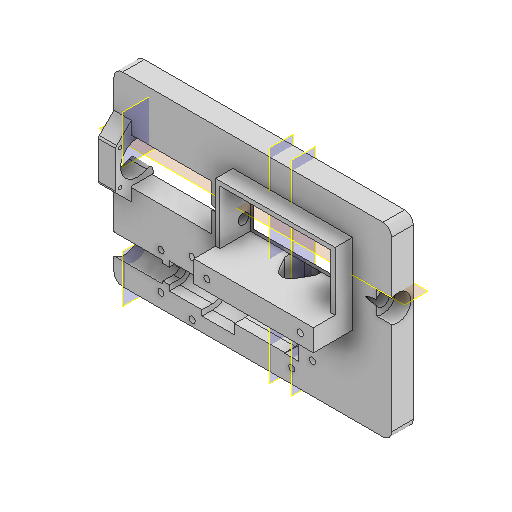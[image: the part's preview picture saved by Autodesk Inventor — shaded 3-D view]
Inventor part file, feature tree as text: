
AUTODESK INVENTOR PART (.ipt)
format: ipt  version: 2022 (Build 260153000, 153)  size: 477,184 bytes
history: native  units: mm
features: sketch x20, extrude x19, reference x11, other x10, plane x8, projected_geometry x7, fillet x2, chamfer x1, mirror x1, hole x1
ambient origin geometry x8: Origin, YZ Plane, XZ Plane, XY Plane, X Axis, Y Axis, Z Axis, Center Point
bodies: Solid1 (feature_tree)
feature tree (80):
  extrude  "Extrusion1"  Depth=10.0mm
  fillet  "Fillet1"  Radius=10.0mm
  extrude  "Extrusion2"  Depth=51.0mm
  extrude  "Extrusion3"  Depth=20.0mm
  plane  "Work Plane1"
  plane  "Work Plane2"
  chamfer  "Chamfer1"  [1 undecoded]
  extrude  "Extrusion4"  Depth=10.0mm
  extrude  "Extrusion5"  Depth=8.0mm
  extrude  "Extrusion6"  Depth=4.0mm TaperAngle=0.0deg
  plane  "Work Plane3"
  extrude  "Extrusion12"  Depth=20.0mm TaperAngle=0.0deg
  extrude  "Extrusion13"  Depth=10.0mm
  mirror  "Mirror1"
  plane  "Work Plane4"
  plane  "Work Plane5"
  extrude  "Extrusion21"  Depth=2.0mm
  extrude  "Extrusion22"  Depth=30.0mm
  plane  "Arbeitsebene7"
  extrude  "Extrusion27"  Depth=7.0mm
  extrude  "Extrusion28"  Depth=10.0mm
  extrude  "Extrusion29"  Depth=6.0mm
  fillet  "Rundung6"  Radius=6.0mm
  sketch  "Skizze32"  dims[d61=30.0mm d62=-0.523599mm d63=12.0mm]
  plane  "Arbeitsebene8"
  extrude  "Extrusion30"  TaperAngle=0.0deg  [1 undecoded]
  extrude  "Extrusion31"  Depth=40.0mm TaperAngle=0.0deg
  extrude  "Extrusion32"  Depth=0.5mm
  extrude  "Extrusion33"  Depth=1.0mm TaperAngle=0.0deg
  sketch  "Skizze36"  dims[d108=6.0mm d109=0.0mm d110=0.0mm]
  plane  "Arbeitsebene9"
  extrude  "Extrusion34"  Depth=8.0mm
  extrude  "Extrusion35"  TaperAngle=45.0deg  [1 undecoded]
  hole  "Bohrung2"  [1 undecoded]
  sketch  "Sketch1"  dims[d0=127.8mm d1=85.5mm d2=10.0mm d3=0.0mm]
  sketch  "Sketch2"  dims[d4=4.0mm d5=51.0mm]
  projected_geometry  "Projected Loop1"
  sketch  "Sketch3"  dims[d6=25.0mm d7=20.0mm]
  projected_geometry  "Projected Loop2"
  sketch  "Sketch4"  dims[d8=15.0mm]
  projected_geometry  "Projected Loop3"
  sketch  "Sketch5"  dims[d9=6.0mm]
  sketch  "Sketch6"  dims[d10=0.0mm]
  reference  "Reference2"
  sketch  "Sketch12"  dims[d11=1.5mm d12=0.0mm d13=0.0mm]
  reference  "Reference4"
  sketch  "Sketch13"  dims[d14=4.0mm d15=2.0mm d16=45.0deg d17=10.0mm]
  sketch  "Sketch22"  dims[d18=8.0mm d19=0.0mm d20=1.9mm]
  projected_geometry  "Projected Loop8"
  sketch  "Sketch23"  dims[d21=4.0mm d22=5.0mm d23=0.0mm]
  projected_geometry  "Projected Loop9"
  reference  "Reference11"
  sketch  "Skizze28"  dims[d27=20.0mm d28=18.0mm d29=0.0mm]
  sketch  "Skizze29"  dims[d38=10.0mm d52=2.0mm]
  reference  "Referenz13"
  sketch  "Skizze30"  dims[d53=2.0mm d54=2.0mm]
  reference  "Referenz14"
  reference  "Referenz16"
  sketch  "Skizze33"  dims[d64=7.0mm d65=0.0mm d100=7.0mm]
  reference  "Referenz17"
  sketch  "Skizze34"  dims[d101=10.0mm d102=0.0mm d103=11.8mm]
  reference  "Referenz18"
  sketch  "Skizze35"  dims[d105=2.8mm d106=2.8mm d107=6.0mm]
  projected_geometry  "Projizierte Kontur15"
  reference  "Referenz19"
  reference  "Referenz20"
  sketch  "Skizze37"  dims[d142=0.5mm d143=40.0mm d144=0.0mm]
  reference  "Referenz21"
  sketch  "Skizze38"  dims[d145=8.0mm d146=0.0mm d147=0.5mm d148=1.0mm d149=0.0mm d150=2.0mm d151=45.0deg d152=45.0deg d153=8.0mm d154=0.0mm d155=7.0mm d156=3.0mm d157=0.0mm d158=30.0mm d159=0.0mm d160=17.0mm d161=15.0mm d162=0.0mm d163=0.5mm d164=15.0mm d165=0.0mm d166=8.0mm d167=10.0mm d168=0.0mm d169=2.8mm d170=6.0mm d171=4.0mm d172=2.0mm d173=90.0deg d174=8.0mm d175=20.594885mm]
  projected_geometry  "Projizierte Kontur16"
  other  "<userpath>\Documents\GitHub\Guinardia\INVENTOR\Assembly_Guinardia_V1.iam"
  other  "Assembly_Guinardia_V1.iam"
  other  "00_CCTV_lens_M12_25mm_5mp:1"
  other  "00_PipetteTip200ul-1:2"
  other  "00_NEMA8:1"
  other  "00_SM05FC2-Step:1"
  other  "00_CCTV_lens_M12_25mm_5mp:2"
  other  "00_HuaweiP30_Telelens_prismonly:1"
  other  "<userpath>\Documents\Inventor\Guinardia\INVENTOR\Assembly_Guinardia_V0.iam"
  other  "Assembly_Guinardia_V0.iam"
note: 4 required parameter values undecoded (feature->parameter linkage not recoverable at this tier; creation-order binding heuristic only, values carry confidence <= 0.55)
